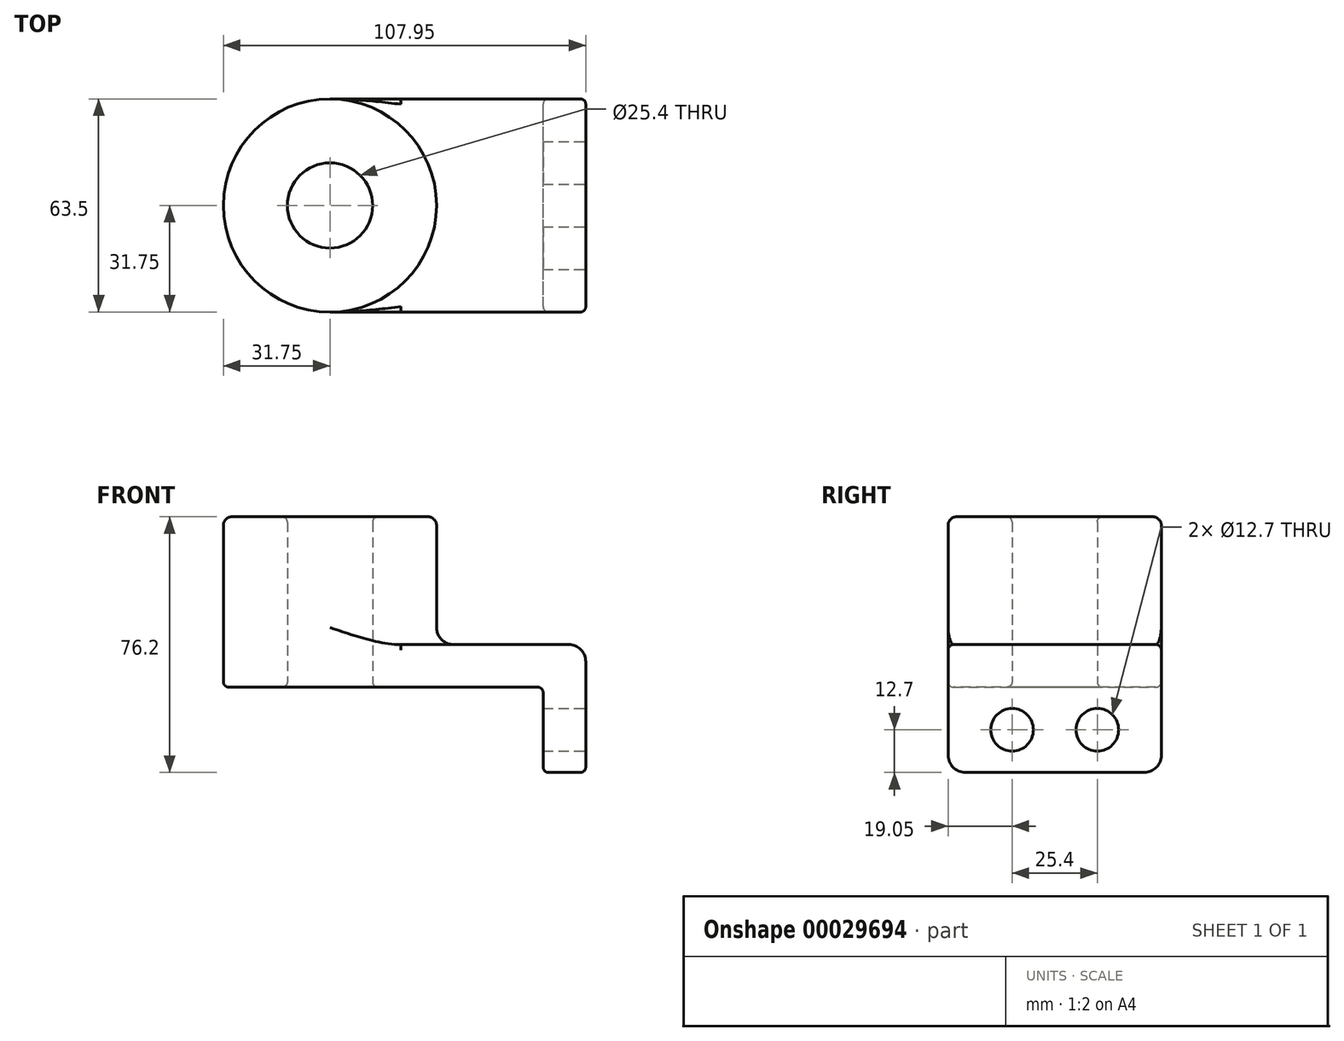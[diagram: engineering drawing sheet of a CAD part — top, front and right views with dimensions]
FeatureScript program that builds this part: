
annotation { "Feature Type Name" : "Feature", "Feature Type Description" : "" }
export const myFeature = defineFeature(function(context is Context, id is Id, definition is map)
    precondition{}
    {
        {
            var Q0;
            Q0=qCreatedBy(makeId("Top.planeOp"),FACE);
            var sketch = newSketch(context, id + "F0", { "sketchPlane" : qUnion([Q0])});
            skLineSegment(sketch, "E0.rect.bottom", {"start": v(-38.1, 31.75) * mm, "end": v(38.1, 31.75) * mm});
            skLineSegment(sketch, "E0.rect.top", {"start": v(-38.1, -31.75) * mm, "end": v(38.1, -31.75) * mm});
            skLineSegment(sketch, "E0.rect.left", {"start": v(-38.1, 31.75) * mm, "end": v(-38.1, -31.75) * mm});
            skLineSegment(sketch, "E0.rect.right", {"start": v(38.1, 31.75) * mm, "end": v(38.1, -31.75) * mm});
            skPoint(sketch, "E0.rect.middle", {"position": v(0, 0) * mm});
            skCircle(sketch, "E1", {"center": v(-38.1, 0) * mm, "radius": 31.75 * mm});
            skCircle(sketch, "E2", {"center": v(-38.1, 0) * mm, "radius": 12.7 * mm});
            skSolve(sketch);
        }
        {
            var Q0;
            Q0 = qSketchRegion(id + "F0", true);
            extrude(context, id + "F1", {"entities" : qUnion([Q0]), "depth" : 12.7 * mm});
        }
        {
            var Q0;
            {var subQ0=sQuery(id+"F0.wireOp",EDGE,"E2");var subQ1=sQuery(id+"F0.wireOp",EDGE,"E0.rect.left");var subQ3=makeQuery(id+"F0.imprint","INTERSECT",VERTEX,{"disambiguationData":[OD(0.0)],"derivedFrom":[subQ1,subQ0]});Q0=makeQuery(id+"F0.imprint","IMPRINT",FACE,{"disambiguationData":[TD([[makeQuery(id+"F0.imprint","IMPRINT",EDGE,{"disambiguationData":[TD([[subQ3,1.0]])],"derivedFrom":subQ0}),-1.0]])]});}
            var Q1;
            {var subQ0=sQuery(id+"F0.wireOp",EDGE,"E2");var subQ1=sQuery(id+"F0.wireOp",EDGE,"E0.rect.left");var subQ3=makeQuery(id+"F0.imprint","INTERSECT",VERTEX,{"disambiguationData":[OD(0.0)],"derivedFrom":[subQ1,subQ0]});Q1=makeQuery(id+"F0.imprint","IMPRINT",FACE,{"disambiguationData":[TD([[makeQuery(id+"F0.imprint","IMPRINT",EDGE,{"disambiguationData":[TD([[subQ3,-1.0]])],"derivedFrom":subQ0}),-1.0]])]});}
            extrude(context, id + "F2", {"entities" : qUnion([Q0, Q1]), "operationType" : NewBodyOperationType.ADD, "depth" : 50.8 * mm});
        }
        {
            var Q0;
            Q0=makeQuery(id+"F1.opExtrude","SWEPT_FACE",FACE,{"disambiguationData":[OSD([sQuery(id+"F0.wireOp",EDGE,"E0.rect.right")])]});
            var sketch = newSketch(context, id + "F3", { "sketchPlane" : qUnion([Q0])});
            skLineSegment(sketch, "E3.bottom", {"start": v(-31.75, 12.7) * mm, "end": v(31.75, 12.7) * mm});
            skLineSegment(sketch, "E3.top", {"start": v(-31.75, -25.4) * mm, "end": v(31.75, -25.4) * mm});
            skLineSegment(sketch, "E3.left", {"start": v(-31.75, 12.7) * mm, "end": v(-31.75, -25.4) * mm});
            skLineSegment(sketch, "E3.right", {"start": v(31.75, 12.7) * mm, "end": v(31.75, -25.4) * mm});
            skCircle(sketch, "E4", {"center": v(-12.7, -12.7) * mm, "radius": 6.35 * mm});
            skLineSegment(sketch, "E5", {"start": v(0, 0) * mm, "end": v(0, -25.4) * mm, "construction": true});
            skCircle(sketch, "E6.MirrorC", {"center": v(12.7, -12.7) * mm, "radius": 6.35 * mm});
            skSolve(sketch);
        }
        {
            var Q0;
            Q0 = qSketchRegion(id + "F3", true);
            extrude(context, id + "F4", {"entities" : qUnion([Q0]), "operationType" : NewBodyOperationType.ADD, "oppositeDirection" : true, "depth" : 12.7 * mm});
        }
        {
            var Q0;
            {var subQ0=sQuery(id+"F0.wireOp",EDGE,"E1");Q0=makeQuery(id+"F2.boolean.opBoolean","INTERSECT",EDGE,{"derivedFrom":[makeQuery(id+"F1.opExtrude","CAP_FACE",FACE,{"disambiguationData":[OSD([sQuery(id+"F0.wireOp",EDGE,"E0.rect.bottom"),sQuery(id+"F0.wireOp",EDGE,"E0.rect.top"),sQuery(id+"F0.wireOp",EDGE,"E0.rect.right"),subQ0,sQuery(id+"F0.wireOp",EDGE,"E2")])],"isStart":false}),makeQuery(id+"F2.opExtrude","SWEPT_FACE",FACE,{"disambiguationData":[OSD([subQ0])]})]});}
            var Q1;
            Q1=makeQuery(id+"F1.opExtrude","CAP_EDGE",EDGE,{"disambiguationData":[OSD([sQuery(id+"F0.wireOp",EDGE,"E0.rect.right")])],"isStart":false});
            var Q2;
            Q2=makeQuery(id+"F4.opExtrude","SWEPT_EDGE",EDGE,{"disambiguationData":[OSD([sQuery(id+"F3.wireOp",EDGE,"E3.top"),sQuery(id+"F3.wireOp",EDGE,"E3.left")])]});
            var Q3;
            Q3=makeQuery(id+"F4.opExtrude","SWEPT_EDGE",EDGE,{"disambiguationData":[OSD([sQuery(id+"F3.wireOp",EDGE,"E3.top"),sQuery(id+"F3.wireOp",EDGE,"E3.right")])]});
            fillet(context, id + "F5", {"entities" : qUnion([Q0, Q1, Q2, Q3]), "radius" : 5.08 * mm, "tangentPropagation" : true, "allowEdgeOverflow" : false});
        }
        {
            var Q0;
            Q0=makeQuery(id+"F1.opExtrude","CAP_EDGE",EDGE,{"disambiguationData":[OSD([sQuery(id+"F0.wireOp",EDGE,"E0.rect.top")])],"isStart":false});
            var Q1;
            Q1=makeQuery(id+"F1.opExtrude","CAP_EDGE",EDGE,{"disambiguationData":[OSD([sQuery(id+"F0.wireOp",EDGE,"E0.rect.top")])],"isStart":true});
            var Q2;
            Q2=makeQuery(id+"F4.opExtrude","CAP_EDGE",EDGE,{"disambiguationData":[OSD([sQuery(id+"F3.wireOp",EDGE,"E3.left")])],"isStart":false});
            var Q3;
            Q3=makeQuery(id+"F4.boolean.opBoolean","INTERSECT",EDGE,{"derivedFrom":[makeQuery(id+"F1.opExtrude","CAP_FACE",FACE,{"disambiguationData":[OSD([sQuery(id+"F0.wireOp",EDGE,"E0.rect.bottom"),sQuery(id+"F0.wireOp",EDGE,"E0.rect.top"),sQuery(id+"F0.wireOp",EDGE,"E0.rect.right"),sQuery(id+"F0.wireOp",EDGE,"E1"),sQuery(id+"F0.wireOp",EDGE,"E2")])],"isStart":true}),makeQuery(id+"F4.opExtrude","CAP_FACE",FACE,{"disambiguationData":[OSD([sQuery(id+"F3.wireOp",EDGE,"E3.bottom"),sQuery(id+"F3.wireOp",EDGE,"E3.top"),sQuery(id+"F3.wireOp",EDGE,"E3.left"),sQuery(id+"F3.wireOp",EDGE,"E3.right"),sQuery(id+"F3.wireOp",EDGE,"E4"),sQuery(id+"F3.wireOp",EDGE,"E6.MirrorC")])],"isStart":false})]});
            var Q4;
            {var subQ0=sQuery(id+"F0.wireOp",EDGE,"E2");Q4=makeQuery(id+"F2.boolean.opBoolean","MERGE",FACE,{"derivedFrom":[makeQuery(id+"F1.opExtrude","SWEPT_FACE",FACE,{"disambiguationData":[OSD([subQ0])]}),makeQuery(id+"F2.opExtrude","SWEPT_FACE",FACE,{"disambiguationData":[OSD([subQ0])]})]});}
            fillet(context, id + "F6", {"entities" : qUnion([Q0, Q1, Q2, Q3, Q4]), "radius" : 1.59 * mm, "tangentPropagation" : true, "allowEdgeOverflow" : false});
        }
        {
            var Q0;
            Q0=makeQuery(id+"F2.opExtrude","CAP_EDGE",EDGE,{"disambiguationData":[OSD([sQuery(id+"F0.wireOp",EDGE,"E1")])],"isStart":false});
            fillet(context, id + "F7", {"entities" : qUnion([Q0]), "radius" : 2.54 * mm, "tangentPropagation" : true, "allowEdgeOverflow" : false});
        }
    });
